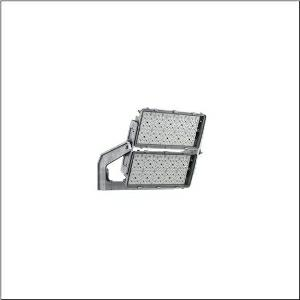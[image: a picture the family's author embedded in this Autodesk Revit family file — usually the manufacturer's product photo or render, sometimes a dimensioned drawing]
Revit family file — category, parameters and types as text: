
# Revit family: floodlight_fl_11_maxi_remote___rs12_5xa779514m01ba_3a09
name_source: partatom
category: Lighting Fixtures
units: mm (PartAtom-declared; Revit-internal decimal feet)

## family parameters
Cut with Voids When Loaded = No
Host = Face
Light Source = No
Part Type = Normal
Room Calculation Point = No
Round Connector Dimension = Use Diameter
Shared = No

## types (1)
- --- (1 x LED, 76660 lm, 707.9 W, 5700K)
    Apparent Load = 708 VA
    CIE Flux Codes = 79 92 99 100 100
    Color Rendering = 90
    Color Temperature = 5700K
    Default Elevation = 1800 mm
    Description = Floodlight FL 11  maxi  Remote floodlight; light control with lens of PMMA; cover panel of toughened safety glass, transparent; light distribution: RS12, rotationally symmetric direct distribution, LEDcolour temperature: 5700K, rated luminous flux: 76.660lm, colour rendering: CRI > 90, light colour: 957; luminous efficacy: 108lm/W; brightness control: DMX+RDM; with terminal, 8-pole, max. 2.5mm², mains connection: 220..240V/380..400V AC, 50/60Hz, surge voltage resistance: line to ground: 10kV, ECG replaceable separately, LED unit replaceable without ESD environment, dustproof LED module, dimming range 10..100%; 708W floodlight with 2x LED unit of diecast aluminium, coated grey; length: 713mm / width: 651mm / height: 338mm; mounting bracket, of diecast aluminium, uncoated, natural, equipment: Longlife, protection rating (complete): IP66; insulation class (complete): insulation class I (protective earthing); certification: CE, ENEC, VDE; ball protection: ball impact resistance with accessories, impact resistance: IK07; only for outdoor installations, rated ambient temperature 10°C, permissible operating ambient temperature: -40..+40°C, permissible storage temperature: -40..+85°Cpackaging unit: 1 piece

Light Distribution: RS12
    Height = 320 mm
    Lamp = 1 x LED
    Lamp Light Flux = 76660 lm
    Lamp Power = 707.9 W
    Lamp count = 1
    Length = 712 mm
    Luminous efficacy = 108 lm/W
    Manufacturer = Siteco
    ModVariant = No
    Model = 5XA779514M01BA
    Mounting Place = Ceiling
    Mounting Type = Surface mounted
    Number of Poles = 1
    OnlyDefault = Yes
    Power Factor = 1
    Product Name = Floodlight FL 11 maxi Remote | RS12
    Product group = floodlight | ceiling mounted
    ProductGroupID = 301
    Protection Class = Protection class I
    Protection Degree = IP 66
    RLX_Detail_Level = 1
    RLX_Emergency_Light_Flux = 0 lm
    RLX_Emergency_Type = 0
    RLX_Emergency_Type_DB = No
    RlxData = <blob elided: 41105 chars, md5=df024ffd>
    Socket = socket
    Standby Power = 0 W
    System Light Flux = 76660 lm
    System Power = 708 W
    Type Comments = factory setting: luminous flux: 100 % | dim-lin: 254 | 740 mA
    Type Image = l_1349125.jpg
    URL = http://relux.com
    VarID = @adj_182050
    Voltage = 0 V
    Weight = 0.00 kg
    Width = 655 mm

## geometry (parser evidence)
native form markers: Blend x4, Sweep x11
no freeform markers — native parametric forms only
